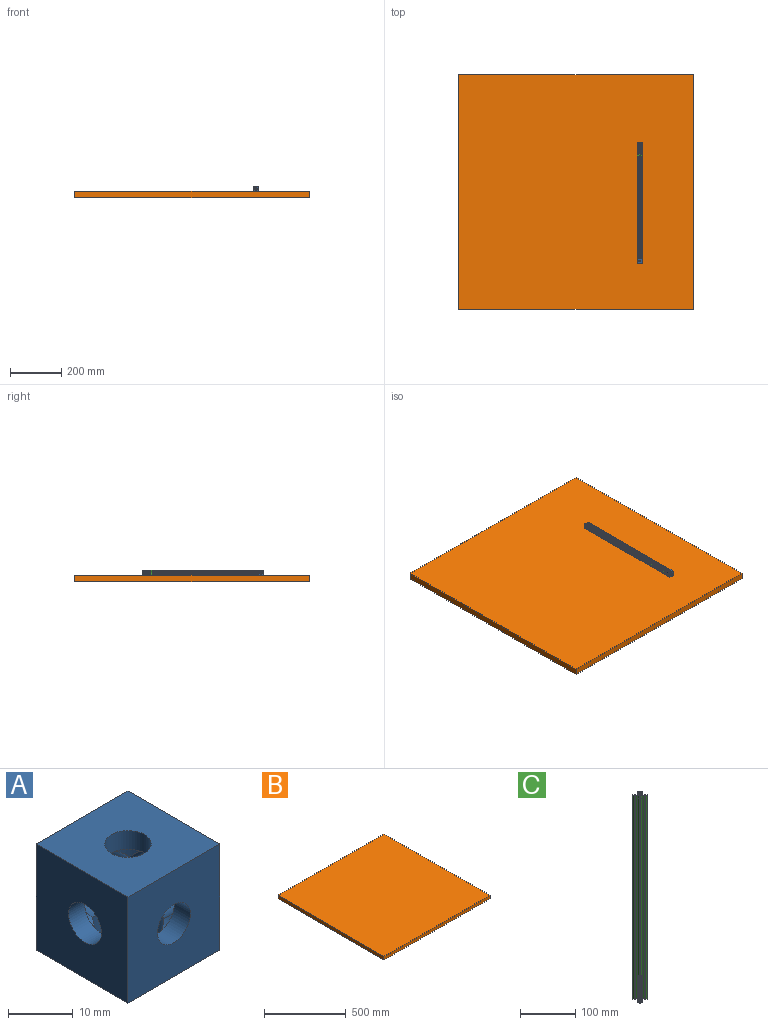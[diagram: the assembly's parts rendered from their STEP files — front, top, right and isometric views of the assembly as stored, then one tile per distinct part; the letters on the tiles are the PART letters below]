
ASSEMBLY  parts=3 mates=4
PART A: 18 faces, bbox 20x20x20 mm
  f0: plane 20x20mm, normal (0,1,0), area 305mm2, adj f3,f4,f6,f7,f13
  f1: cylinder r=5.5mm len=11mm, axis (0,0,-1), area 48.2mm2, adj f9,f11,f13,f15,f17
  f2: plane 20x20mm, normal (0,-1,0), area 360mm2, adj f3,f4,f6,f7,f10
  f3: plane 20x20mm, normal (1,0,0), area 305mm2, adj f0,f2,f6,f7,f17
  f4: plane 20x20mm, normal (-1,0,0), area 360mm2, adj f0,f2,f6,f7,f14
  f5: cylinder r=3.57mm len=7.14mm, axis (0,0,-1), area 78.5mm2, adj f6,f9
  f6: plane 20x20mm, normal (0,0,1), area 360mm2, adj f0,f2,f3,f4,f5
  f7: plane 20x20mm, normal (0,0,-1), area 305mm2, adj f0,f2,f3,f4,f8
  f8: cylinder r=5.5mm len=11mm, axis (0,0,-1), area 180.2mm2, adj f7,f11,f13,f15,f17
  f9: plane 11x11mm, normal (0,0,-1), area 55mm2, adj f1,f5
  f10: cylinder r=3.57mm len=7.14mm, axis (0,1,0), area 78.5mm2, adj f2,f12
  f11: cylinder r=5.5mm len=11mm, axis (0,1,0), area 42mm2, adj f1,f8,f12,f15,f17
  f12: plane 11x11mm, normal (0,1,0), area 55mm2, adj f10,f11
  f13: cylinder r=5.5mm len=11mm, axis (0,1,0), area 184.9mm2, adj f0,f1,f8,f15,f17
  f14: cylinder r=3.57mm len=7.14mm, axis (1,0,0), area 78.5mm2, adj f4,f16
  f15: cylinder r=5.5mm len=11mm, axis (1,0,0), area 54mm2, adj f1,f8,f11,f13,f16
  f16: plane 11x11mm, normal (1,0,0), area 55mm2, adj f14,f15
  f17: cylinder r=5.5mm len=11mm, axis (1,0,0), area 174.9mm2, adj f1,f3,f8,f11,f13
PART B: 6 faces, bbox 914.4x914.4x25.4 mm
  f0: plane 914.4x25.4mm, normal (0,-1,0), area 23225.8mm2, adj f1,f3,f4,f5
  f1: plane 914.4x25.4mm, normal (1,0,0), area 23225.8mm2, adj f0,f2,f4,f5
  f2: plane 914.4x25.4mm, normal (0,1,0), area 23225.8mm2, adj f1,f3,f4,f5
  f3: plane 914.4x25.4mm, normal (-1,0,0), area 23225.8mm2, adj f0,f2,f4,f5
  f4: plane 914.4x914.4mm, normal (0,0,-1), area 836127.4mm2, adj f0,f1,f2,f3
  f5: plane 914.4x914.4mm, normal (0,0,1), area 836127.4mm2, adj f0,f1,f2,f3
PART C: 87 faces, bbox 20x20x450 mm
  f0: plane 450x0.54mm, normal (-1,0,0), area 243mm2, adj f1,f79,f85,f86
  f1: plane 450x1.63mm, normal (0,1,0), area 733.5mm2, adj f0,f2,f85,f86
  f2: plane 450x1.63mm, normal (1,0,0), area 733.5mm2, adj f1,f3,f85,f86
  f3: plane 450x0.54mm, normal (0,-1,0), area 243mm2, adj f2,f79,f85,f86
  f4: plane 450x0.54mm, normal (1,0,0), area 243mm2, adj f5,f80,f85,f86
  f5: plane 450x1.09mm, normal (0.71,-0.71,0), area 693.7mm2, adj f4,f6,f85,f86
  f6: plane 450x0.54mm, normal (0,-1,0), area 243mm2, adj f5,f7,f85,f86
  f7: plane 450x1.63mm, normal (-1,0,0), area 733.5mm2, adj f6,f80,f85,f86
  f8: plane 450x0.54mm, normal (1,0,0), area 243mm2, adj f9,f81,f85,f86
  f9: plane 450x1.63mm, normal (0,-1,0), area 733.5mm2, adj f8,f10,f85,f86
  f10: plane 450x1.63mm, normal (-1,0,0), area 733.5mm2, adj f9,f11,f85,f86
  f11: plane 450x0.54mm, normal (0,1,0), area 243mm2, adj f10,f81,f85,f86
  f12: plane 450x0.54mm, normal (-1,0,0), area 243mm2, adj f13,f82,f85,f86
  f13: plane 450x1.09mm, normal (-0.71,0.71,0), area 693.7mm2, adj f12,f14,f85,f86
  f14: plane 450x0.54mm, normal (0,1,0), area 243mm2, adj f13,f15,f85,f86
  f15: plane 450x1.63mm, normal (1,0,0), area 733.5mm2, adj f14,f82,f85,f86
  f16: plane 450x2.61mm, normal (1,0,0), area 1174.5mm2, adj f17,f83,f85,f86
  f17: plane 450x1.64mm, normal (0,-1,0), area 737.7mm2, adj f16,f18,f85,f86
  f18: plane 450x3.16mm, normal (-0.71,-0.71,0), area 2011.4mm2, adj f17,f19,f85,f86
  f19: plane 450x4.68mm, normal (-1,0,0), area 2105.4mm2, adj f18,f20,f85,f86
  f20: plane 450x3.16mm, normal (-0.71,0.71,0), area 2011.4mm2, adj f19,f21,f85,f86
  f21: plane 450x1.64mm, normal (0,1,0), area 737.7mm2, adj f20,f22,f85,f86
  f22: plane 450x2.61mm, normal (1,0,0), area 1174.5mm2, adj f21,f23,f85,f86
  f23: plane 450x0.11mm, normal (0,1,0), area 49.5mm2, adj f22,f24,f85,f86
  f24: plane 450x1.46mm, normal (-0.71,0.71,0), area 928.3mm2, adj f23,f25,f85,f86
  f25: cylinder r=0.79mm len=450mm, axis (0,0,-1), area 279.2mm2, adj f24,f26,f85,f86
  f26: plane 450x3.59mm, normal (-1,0,0), area 1616.7mm2, adj f25,f27,f85,f86
  f27: cylinder r=1.5mm len=450mm, axis (0,0,-1), area 1060.3mm2, adj f26,f28,f85,f86
  f28: plane 450x3.59mm, normal (0,-1,0), area 1616.7mm2, adj f27,f29,f85,f86
  f29: cylinder r=0.79mm len=450mm, axis (0,0,-1), area 279.2mm2, adj f28,f30,f85,f86
  f30: plane 450x1.46mm, normal (0.71,-0.71,0), area 928.3mm2, adj f29,f31,f85,f86
  f31: plane 450x0.11mm, normal (1,0,0), area 49.5mm2, adj f30,f32,f85,f86
  f32: plane 450x2.61mm, normal (0,1,0), area 1174.5mm2, adj f31,f33,f85,f86
  f33: plane 450x1.64mm, normal (1,0,0), area 737.7mm2, adj f32,f34,f85,f86
  f34: plane 450x3.16mm, normal (0.71,-0.71,0), area 2011.4mm2, adj f33,f35,f85,f86
  f35: plane 450x4.68mm, normal (0,-1,0), area 2105.4mm2, adj f34,f36,f85,f86
  f36: plane 450x3.16mm, normal (-0.71,-0.71,0), area 2011.4mm2, adj f35,f37,f85,f86
  f37: plane 450x1.64mm, normal (-1,0,0), area 737.7mm2, adj f36,f38,f85,f86
  f38: plane 450x2.61mm, normal (0,1,0), area 1174.5mm2, adj f37,f39,f85,f86
  f39: plane 450x0.11mm, normal (-1,0,0), area 49.5mm2, adj f38,f40,f85,f86
  f40: plane 450x1.46mm, normal (-0.71,-0.71,0), area 928.3mm2, adj f39,f41,f85,f86
  f41: cylinder r=0.79mm len=450mm, axis (0,0,-1), area 279.2mm2, adj f40,f42,f85,f86
  f42: plane 450x3.59mm, normal (0,-1,0), area 1616.7mm2, adj f41,f43,f85,f86
  f43: cylinder r=1.5mm len=450mm, axis (0,0,-1), area 1060.3mm2, adj f42,f44,f85,f86
  f44: plane 450x3.59mm, normal (1,0,0), area 1616.7mm2, adj f43,f45,f85,f86
  f45: cylinder r=0.79mm len=450mm, axis (0,0,-1), area 279.2mm2, adj f44,f46,f85,f86
  f46: plane 450x1.46mm, normal (0.71,0.71,0), area 928.3mm2, adj f45,f47,f85,f86
  f47: plane 450x0.11mm, normal (0,1,0), area 49.5mm2, adj f46,f48,f85,f86
  f48: plane 450x2.61mm, normal (-1,0,0), area 1174.5mm2, adj f47,f49,f85,f86
  f49: plane 450x1.64mm, normal (0,1,0), area 737.7mm2, adj f48,f50,f85,f86
  f50: plane 450x3.16mm, normal (0.71,0.71,0), area 2011.4mm2, adj f49,f51,f85,f86
  f51: plane 450x4.68mm, normal (1,0,0), area 2105.4mm2, adj f50,f52,f85,f86
  f52: plane 450x3.16mm, normal (0.71,-0.71,0), area 2011.4mm2, adj f51,f53,f85,f86
  f53: plane 450x1.64mm, normal (0,-1,0), area 737.7mm2, adj f52,f54,f85,f86
  f54: plane 450x2.61mm, normal (-1,0,0), area 1174.5mm2, adj f53,f55,f85,f86
  f55: plane 450x0.11mm, normal (0,-1,0), area 49.5mm2, adj f54,f56,f85,f86
  f56: plane 450x1.46mm, normal (0.71,-0.71,0), area 928.3mm2, adj f55,f57,f85,f86
  f57: cylinder r=0.79mm len=450mm, axis (0,0,-1), area 279.2mm2, adj f56,f58,f85,f86
  f58: plane 450x3.59mm, normal (1,0,0), area 1616.7mm2, adj f57,f59,f85,f86
  f59: cylinder r=1.5mm len=450mm, axis (0,0,-1), area 1060.3mm2, adj f58,f60,f85,f86
  f60: plane 450x3.59mm, normal (0,1,0), area 1616.7mm2, adj f59,f61,f85,f86
  f61: cylinder r=0.79mm len=450mm, axis (0,0,-1), area 279.2mm2, adj f60,f62,f85,f86
  f62: plane 450x1.46mm, normal (-0.71,0.71,0), area 928.3mm2, adj f61,f63,f85,f86
  f63: plane 450x0.11mm, normal (-1,0,0), area 49.5mm2, adj f62,f64,f85,f86
  f64: plane 450x2.61mm, normal (0,-1,0), area 1174.5mm2, adj f63,f65,f85,f86
  f65: plane 450x1.64mm, normal (-1,0,0), area 737.7mm2, adj f64,f66,f85,f86
  f66: plane 450x3.16mm, normal (-0.71,0.71,0), area 2011.4mm2, adj f65,f67,f85,f86
  f67: plane 450x4.68mm, normal (0,1,0), area 2105.4mm2, adj f66,f68,f85,f86
  f68: plane 450x3.16mm, normal (0.71,0.71,0), area 2011.4mm2, adj f67,f69,f85,f86
  f69: plane 450x1.64mm, normal (1,0,0), area 737.7mm2, adj f68,f70,f85,f86
  f70: plane 450x2.61mm, normal (0,-1,0), area 1174.5mm2, adj f69,f71,f85,f86
  f71: plane 450x0.11mm, normal (1,0,0), area 49.5mm2, adj f70,f72,f85,f86
  f72: plane 450x1.46mm, normal (0.71,0.71,0), area 928.3mm2, adj f71,f73,f85,f86
  f73: cylinder r=0.79mm len=450mm, axis (0,0,-1), area 279.2mm2, adj f72,f74,f85,f86
  f74: plane 450x3.59mm, normal (0,1,0), area 1616.7mm2, adj f73,f75,f85,f86
  f75: cylinder r=1.5mm len=450mm, axis (0,0,-1), area 1060.3mm2, adj f74,f76,f85,f86
  f76: plane 450x3.59mm, normal (-1,0,0), area 1616.7mm2, adj f75,f77,f85,f86
  f77: cylinder r=0.79mm len=450mm, axis (0,0,-1), area 279.2mm2, adj f76,f78,f85,f86
  f78: plane 450x1.46mm, normal (-0.71,-0.71,0), area 928.3mm2, adj f77,f83,f85,f86
  f79: plane 450x1.09mm, normal (-0.71,-0.71,0), area 693.7mm2, adj f0,f3,f85,f86
  f80: plane 450x1.63mm, normal (0,1,0), area 733.5mm2, adj f4,f7,f85,f86
  f81: plane 450x1.09mm, normal (0.71,0.71,0), area 693.7mm2, adj f8,f11,f85,f86
  f82: plane 450x1.63mm, normal (0,-1,0), area 733.5mm2, adj f12,f15,f85,f86
  f83: plane 450x0.11mm, normal (0,-1,0), area 49.5mm2, adj f16,f78,f85,f86
  f84: cylinder r=2.1mm len=450mm, axis (0,0,-1), area 5937.6mm2, adj f85,f86
  f85: plane 20x20mm, normal (0,0,1), area 151.6mm2, adj f0,f1,f2,f3,f4,f5,f6,f7
  f86: plane 20x20mm, normal (0,0,-1), area 151.6mm2, adj f0,f1,f2,f3,f4,f5,f6,f7
PLACE A rot(axis=(0,0,-1),90deg) t=(705.8,188.22,0)mm
PLACE B t=(457.2,457.2,0)mm
PLACE C rot(axis=(-1,0,0),90deg) t=(705.16,198.22,10.32)mm
MATE planar C.f84 <-> A.f4  axis (0,-1,0) through (705.16,198.22,10.32)mm
MATE planar A.f1 <-> B.f5  axis (0,0,-1) through (705.8,188.22,0)mm
MATE parallel A.f3 <-> B.f0  axis (0,-1,0) through (706,178.22,9.9)mm
MATE slider C.f84 <-> A.f14  axis (0,-1,0) through (705.16,198.22,10.32)mm
